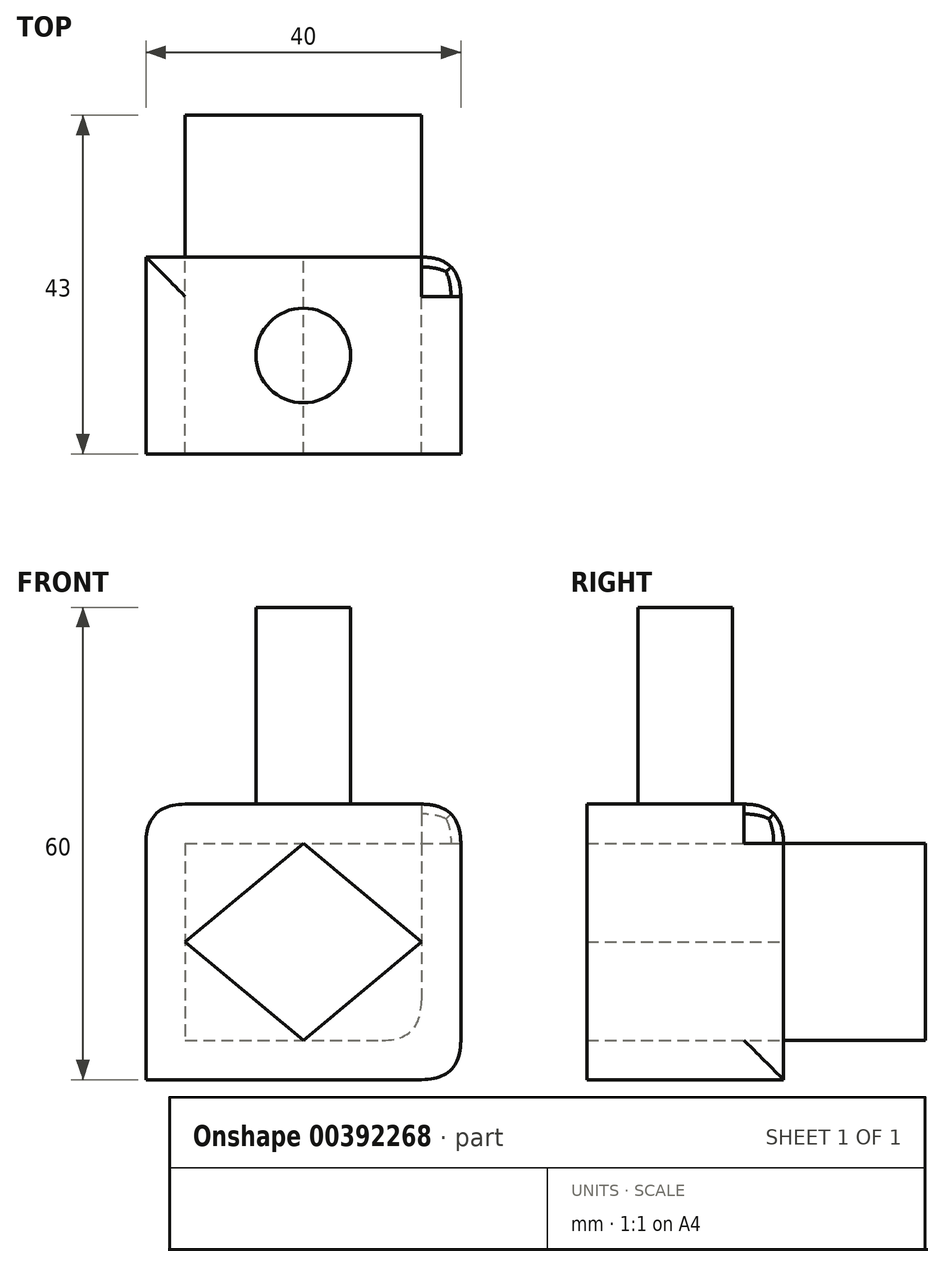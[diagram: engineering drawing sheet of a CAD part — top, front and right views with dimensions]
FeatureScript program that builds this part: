
annotation { "Feature Type Name" : "Feature", "Feature Type Description" : "" }
export const myFeature = defineFeature(function(context is Context, id is Id, definition is map)
    precondition{}
    {
        {
            var Q0;
            Q0=qCreatedBy(makeId("Top.planeOp"),FACE);
            var sketch = newSketch(context, id + "F0", { "sketchPlane" : qUnion([Q0])});
            skLineSegment(sketch, "E0.bottom", {"start": v(0, 0) * mm, "end": v(30, 0) * mm});
            skLineSegment(sketch, "E0.top", {"start": v(0, 18) * mm, "end": v(30, 18) * mm});
            skLineSegment(sketch, "E0.left", {"start": v(0, 0) * mm, "end": v(0, 18) * mm});
            skLineSegment(sketch, "E0.right", {"start": v(30, 0) * mm, "end": v(30, 18) * mm});
            skPoint(sketch, "E1.firstSnap0", {"position": v(0, 9) * mm});
            skPoint(sketch, "E1.oppositeSnap0", {"position": v(0, 9) * mm});
            skSolve(sketch);
        }
        {
            var Q0;
            Q0=makeQuery(id+"F0.imprint","IMPRINT",FACE,{"disambiguationData":[TD([[makeQuery(id+"F0.imprint","IMPRINT",EDGE,{"derivedFrom":sQuery(id+"F0.wireOp",EDGE,"E0.bottom")}),1.0]])]});
            extrude(context, id + "F1", {"entities" : qUnion([Q0]), "depth" : 25 * mm});
        }
        {
            var Q0;
            Q0=makeQuery(id+"F1.opExtrude","SWEPT_FACE",FACE,{"disambiguationData":[OSD([sQuery(id+"F0.wireOp",EDGE,"E0.bottom")])]});
            var sketch = newSketch(context, id + "F2", { "sketchPlane" : qUnion([Q0])});
            skLineSegment(sketch, "E2", {"start": v(0, 12.5) * mm, "end": v(15, 25) * mm});
            skLineSegment(sketch, "E3", {"start": v(15, 25) * mm, "end": v(30, 12.5) * mm});
            skLineSegment(sketch, "E4", {"start": v(0, 12.5) * mm, "end": v(15, 0) * mm});
            skLineSegment(sketch, "E5", {"start": v(15, 0) * mm, "end": v(30, 12.5) * mm});
            skLineSegment(sketch, "E6.0", {"start": v(-5, -5) * mm, "end": v(35, -5) * mm});
            skLineSegment(sketch, "E6.1", {"start": v(-5, 30) * mm, "end": v(-5, -5) * mm});
            skLineSegment(sketch, "E6.2", {"start": v(35, 30) * mm, "end": v(-5, 30) * mm});
            skLineSegment(sketch, "E6.3", {"start": v(35, -5) * mm, "end": v(35, 30) * mm});
            skSolve(sketch);
        }
        {
            var Q0;
            Q0 = qSketchRegion(id + "F2", true);
            extrude(context, id + "F3", {"entities" : qUnion([Q0]), "depth" : 25 * mm});
        }
        {
            var Q0;
            Q0=makeQuery(id+"F3.opExtrude","SWEPT_FACE",FACE,{"disambiguationData":[OSD([sQuery(id+"F2.wireOp",EDGE,"E6.2")])]});
            var sketch = newSketch(context, id + "F4", { "sketchPlane" : qUnion([Q0])});
            skCircle(sketch, "E7", {"center": v(15, -12.5) * mm, "radius": 6.01 * mm});
            skPoint(sketch, "E7.centerSnap0", {"position": v(-5, -12.5) * mm});
            skPoint(sketch, "E7.centerSnap1", {"position": v(15, 0) * mm});
            skSolve(sketch);
        }
        {
            var Q0;
            Q0 = qSketchRegion(id + "F4", true);
            extrude(context, id + "F5", {"entities" : qUnion([Q0]), "operationType" : NewBodyOperationType.ADD, "depth" : 25 * mm});
        }
        {
            var Q0;
            Q0=makeQuery(id+"F3.opExtrude","SWEPT_EDGE",EDGE,{"disambiguationData":[OSD([sQuery(id+"F2.wireOp",EDGE,"E6.2"),sQuery(id+"F2.wireOp",EDGE,"E6.3")])]});
            var Q1;
            Q1=makeQuery(id+"F3.opExtrude","SWEPT_EDGE",EDGE,{"disambiguationData":[OSD([sQuery(id+"F2.wireOp",EDGE,"E6.0"),sQuery(id+"F2.wireOp",EDGE,"E6.3")])]});
            var Q2;
            Q2=makeQuery(id+"F3.opExtrude","SWEPT_EDGE",EDGE,{"disambiguationData":[OSD([sQuery(id+"F2.wireOp",EDGE,"E6.1"),sQuery(id+"F2.wireOp",EDGE,"E6.2")])]});
            var Q3;
            Q3=makeQuery(id+"F3.opExtrude","CAP_EDGE",EDGE,{"disambiguationData":[OSD([sQuery(id+"F2.wireOp",EDGE,"E6.2")])],"isStart":true});
            var Q4;
            Q4=makeQuery(id+"F3.opExtrude","CAP_EDGE",EDGE,{"disambiguationData":[OSD([sQuery(id+"F2.wireOp",EDGE,"E6.3")])],"isStart":true});
            var Q5;
            Q5=makeQuery(id+"F1.opExtrude","CAP_EDGE",EDGE,{"disambiguationData":[OSD([sQuery(id+"F0.wireOp",EDGE,"E0.right")])],"isStart":true});
            fillet(context, id + "F6", {"entities" : qUnion([Q0, Q1, Q2, Q3, Q4, Q5]), "radius" : 5 * mm, "tangentPropagation" : true, "rho" : 0.5, "crossSection" : FilletCrossSection.CONIC, "allowEdgeOverflow" : false});
        }
    });
